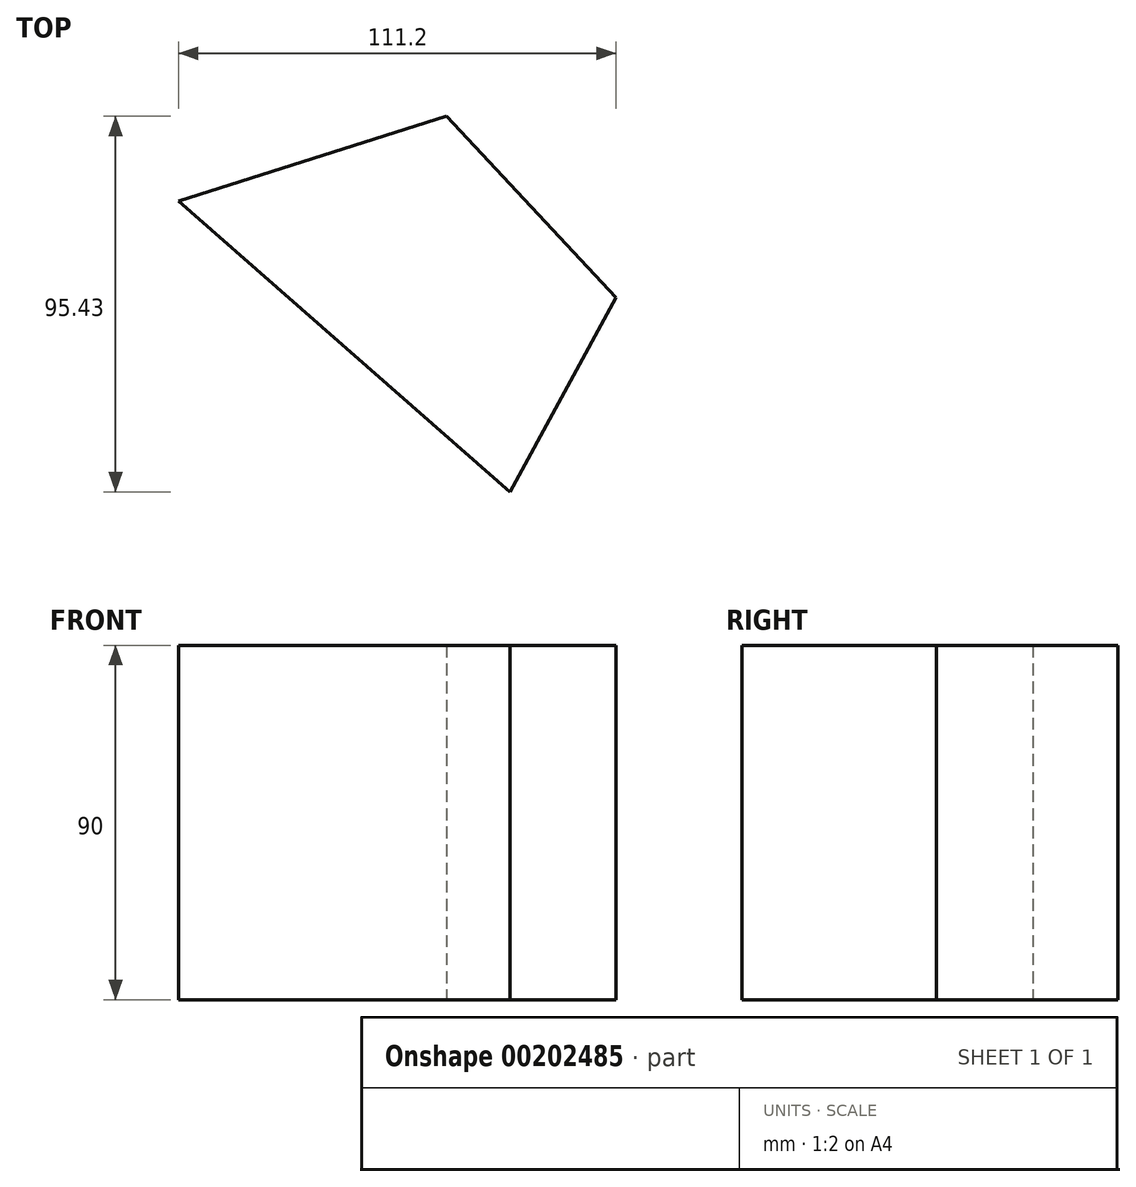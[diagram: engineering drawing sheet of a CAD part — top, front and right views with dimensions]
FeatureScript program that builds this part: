
annotation { "Feature Type Name" : "Feature", "Feature Type Description" : "" }
export const myFeature = defineFeature(function(context is Context, id is Id, definition is map)
    precondition{}
    {
        {
            var Q0;
            Q0=qCreatedBy(makeId("Top.planeOp"),FACE);
            var sketch = newSketch(context, id + "F0", { "sketchPlane" : qUnion([Q0])});
            skLineSegment(sketch, "E0", {"start": v(-52.2, 30.28) * mm, "end": v(15.85, 51.86) * mm});
            skLineSegment(sketch, "E1", {"start": v(15.85, 51.86) * mm, "end": v(59, 5.8) * mm});
            skLineSegment(sketch, "E2", {"start": v(59, 5.8) * mm, "end": v(32.03, -43.57) * mm});
            skLineSegment(sketch, "E3", {"start": v(32.03, -43.57) * mm, "end": v(-52.2, 30.28) * mm});
            skSolve(sketch);
        }
        {
            var Q0;
            Q0=makeQuery(id+"F0.imprint","IMPRINT",FACE,{"disambiguationData":[TD([[makeQuery(id+"F0.imprint","IMPRINT",EDGE,{"derivedFrom":sQuery(id+"F0.wireOp",EDGE,"E0")}),-1.0]])]});
            extrude(context, id + "F1", {"entities" : qUnion([Q0]), "depth" : 90 * mm});
        }
    });
